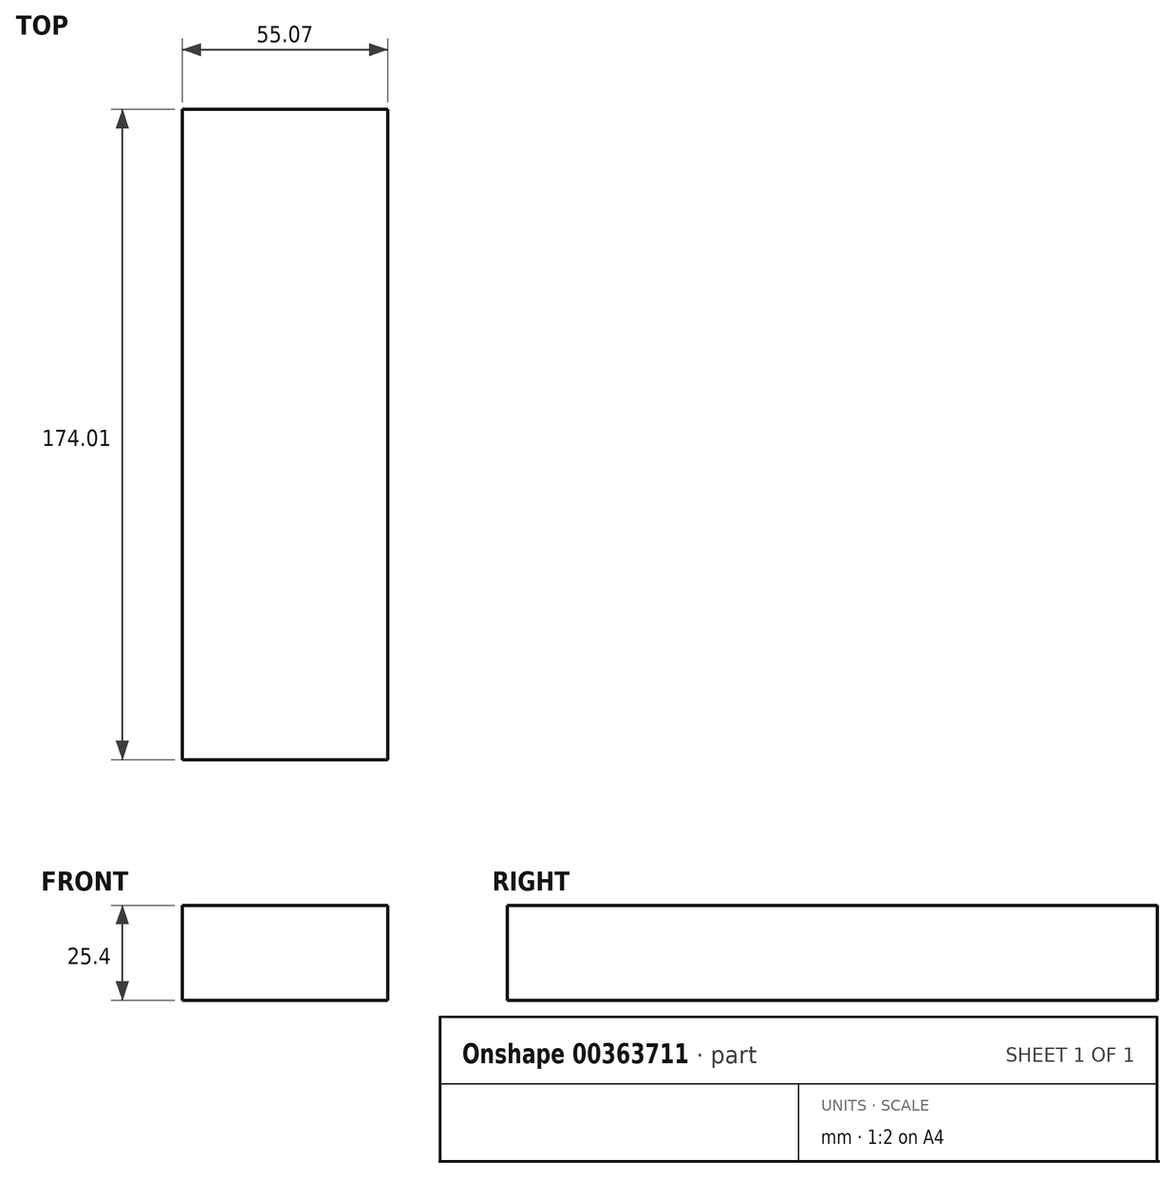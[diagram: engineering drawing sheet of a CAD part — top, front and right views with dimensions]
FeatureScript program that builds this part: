
annotation { "Feature Type Name" : "Feature", "Feature Type Description" : "" }
export const myFeature = defineFeature(function(context is Context, id is Id, definition is map)
    precondition{}
    {
        {
            var Q0;
            Q0=qCreatedBy(makeId("Top.planeOp"),FACE);
            var sketch = newSketch(context, id + "F0", { "sketchPlane" : qUnion([Q0])});
            skCircle(sketch, "E0", {"center": v(0, 0) * mm, "radius": 22.64 * mm});
            skSolve(sketch);
        }
        {
            var Q0;
            Q0=qCreatedBy(makeId("Top.planeOp"),FACE);
            var sketch = newSketch(context, id + "F1", { "sketchPlane" : qUnion([Q0])});
            skLineSegment(sketch, "E1.bottom", {"start": v(0, 0) * mm, "end": v(-55.07, 0) * mm});
            skLineSegment(sketch, "E1.top", {"start": v(0, 174.01) * mm, "end": v(-55.07, 174.01) * mm});
            skLineSegment(sketch, "E1.left", {"start": v(0, 0) * mm, "end": v(0, 174.01) * mm});
            skLineSegment(sketch, "E1.right", {"start": v(-55.07, 0) * mm, "end": v(-55.07, 174.01) * mm});
            skSolve(sketch);
        }
        {
            var Q0;
            Q0=makeQuery(id+"F1.imprint","IMPRINT",FACE,{"disambiguationData":[TD([[makeQuery(id+"F1.imprint","IMPRINT",EDGE,{"derivedFrom":sQuery(id+"F1.wireOp",EDGE,"E1.bottom")}),-1.0]])]});
            extrude(context, id + "F2", {"entities" : qUnion([Q0]), "depth" : 25.4 * mm});
        }
        {
            var Q0;
            Q0=sQuery(id+"F0.wireOp",EDGE,"E0");
            extrude(context, id + "F3", {"bodyType" : ToolBodyType.SURFACE, "surfaceEntities" : qUnion([Q0]), "depth" : 111.64 * mm});
        }
    });
